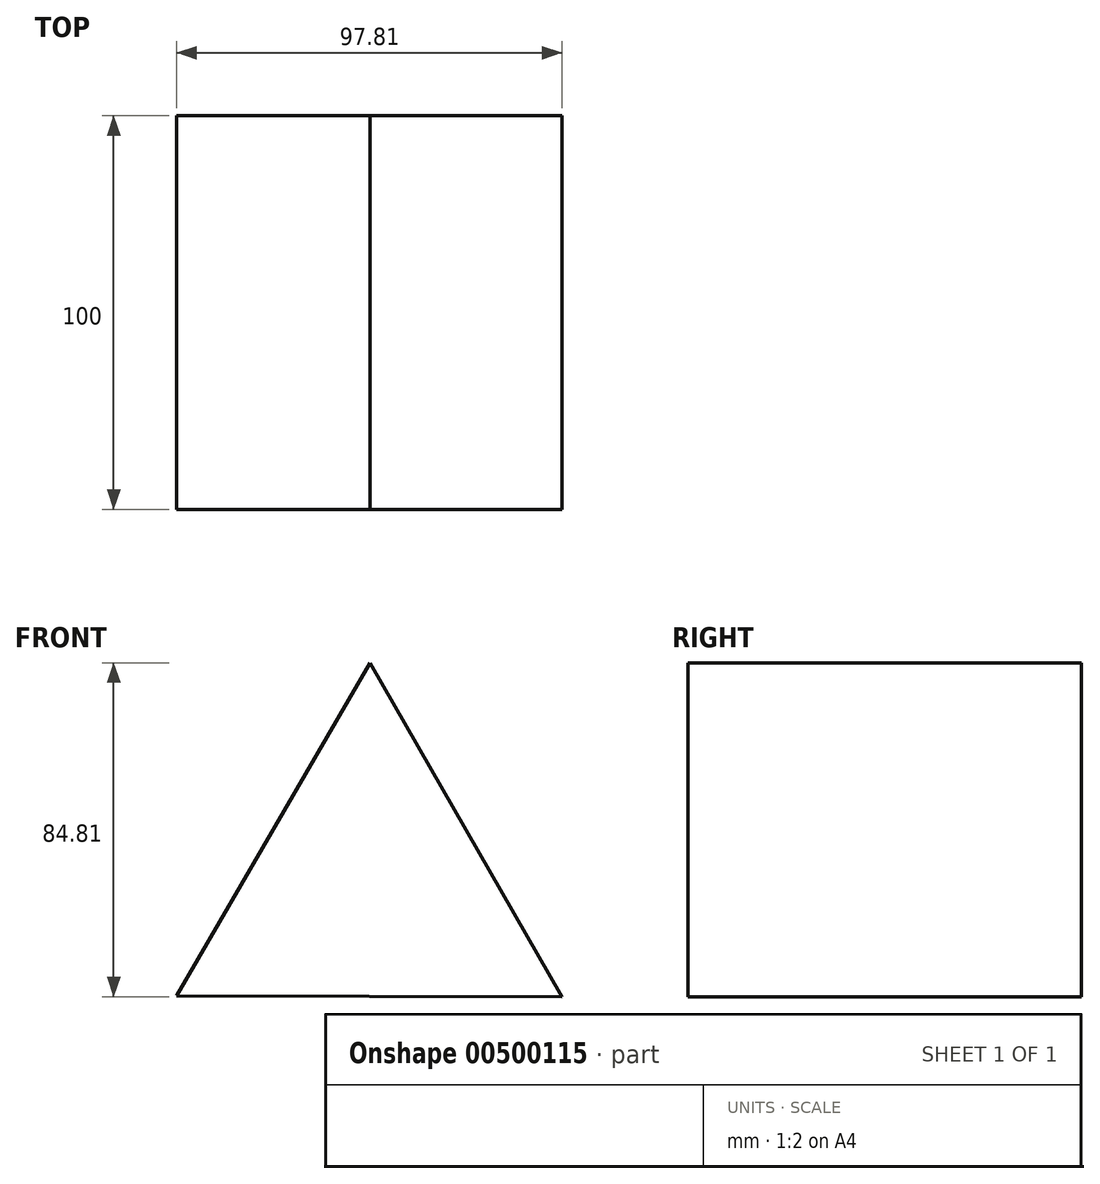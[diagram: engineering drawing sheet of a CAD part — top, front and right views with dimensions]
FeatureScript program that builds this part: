
annotation { "Feature Type Name" : "Feature", "Feature Type Description" : "" }
export const myFeature = defineFeature(function(context is Context, id is Id, definition is map)
    precondition{}
    {
        {
            var Q0;
            Q0=qCreatedBy(makeId("Front.planeOp"),FACE);
            var sketch = newSketch(context, id + "F0", { "sketchPlane" : qUnion([Q0])});
            skCircle(sketch, "E0.cCircle", {"center": v(0, 0) * mm, "radius": 56.47 * mm, "construction": true});
            skLineSegment(sketch, "E0.0", {"start": v(0.12, 56.47) * mm, "end": v(48.84, -28.34) * mm});
            skLineSegment(sketch, "E0.1", {"start": v(48.84, -28.34) * mm, "end": v(-48.97, -28.13) * mm});
            skLineSegment(sketch, "E0.2", {"start": v(-48.97, -28.13) * mm, "end": v(0.12, 56.47) * mm});
            skSolve(sketch);
        }
        {
            var Q0;
            Q0=makeQuery(id+"F0.imprint","IMPRINT",FACE,{"disambiguationData":[TD([[makeQuery(id+"F0.imprint","IMPRINT",EDGE,{"derivedFrom":sQuery(id+"F0.wireOp",EDGE,"E0.0")}),-1.0]])]});
            extrude(context, id + "F1", {"entities" : qUnion([Q0]), "endBound" : BoundingType.SYMMETRIC, "depth" : 100 * mm});
        }
    });
